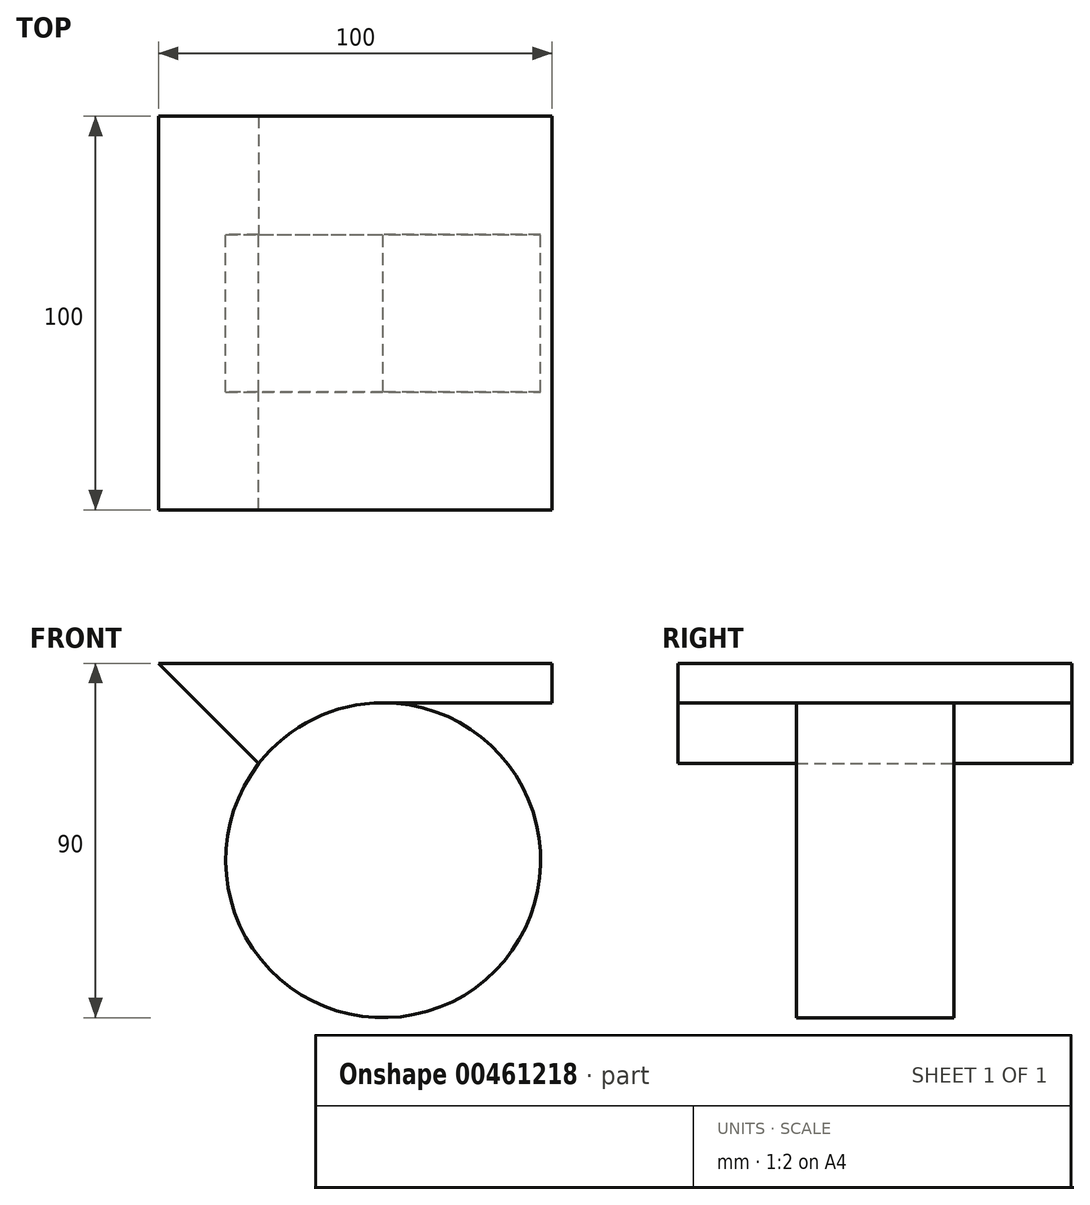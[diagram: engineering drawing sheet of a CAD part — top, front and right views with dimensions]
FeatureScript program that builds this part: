
annotation { "Feature Type Name" : "Feature", "Feature Type Description" : "" }
export const myFeature = defineFeature(function(context is Context, id is Id, definition is map)
    precondition{}
    {
        {
            var Q0;
            Q0=qCreatedBy(makeId("Front.planeOp"),FACE);
            var sketch = newSketch(context, id + "F0", { "sketchPlane" : qUnion([Q0])});
            skArc(sketch, "E0", {"start": v(-31.58, 24.54) * mm, "mid": v(17.58, -35.93) * mm, "end": v(0, 40) * mm});
            skLineSegment(sketch, "E1", {"start": v(0, 40) * mm, "end": v(42.96, 40) * mm});
            skLineSegment(sketch, "E2", {"start": v(42.96, 40) * mm, "end": v(42.96, 50) * mm});
            skLineSegment(sketch, "E3", {"start": v(42.96, 50) * mm, "end": v(-57.04, 50) * mm});
            skLineSegment(sketch, "E4", {"start": v(-57.04, 50) * mm, "end": v(-31.58, 24.54) * mm});
            skSolve(sketch);
        }
        {
            var Q0;
            Q0=makeQuery(id+"F0.imprint","IMPRINT",FACE,{"disambiguationData":[TD([[makeQuery(id+"F0.imprint","IMPRINT",EDGE,{"derivedFrom":sQuery(id+"F0.wireOp",EDGE,"E0")}),1.0]])]});
            extrude(context, id + "F1", {"entities" : qUnion([Q0]), "depth" : 40 * mm});
        }
        {
            var Q0;
            Q0=makeQuery(id+"F1.opExtrude","CAP_FACE",FACE,{"disambiguationData":[OSD([sQuery(id+"F0.wireOp",EDGE,"E0"),sQuery(id+"F0.wireOp",EDGE,"E1"),sQuery(id+"F0.wireOp",EDGE,"E2"),sQuery(id+"F0.wireOp",EDGE,"E3"),sQuery(id+"F0.wireOp",EDGE,"E4")])],"isStart":false});
            var sketch = newSketch(context, id + "F2", { "sketchPlane" : qUnion([Q0])});
            skCircle(sketch, "E5", {"center": v(0, 0) * mm, "radius": 40 * mm});
            skLineSegment(sketch, "E6", {"start": v(0, 40) * mm, "end": v(42.96, 40) * mm});
            skLineSegment(sketch, "E7", {"start": v(42.96, 40) * mm, "end": v(42.96, 50) * mm});
            skLineSegment(sketch, "E8", {"start": v(42.96, 50) * mm, "end": v(-57.04, 50) * mm});
            skLineSegment(sketch, "E9", {"start": v(-57.04, 50) * mm, "end": v(-31.58, 24.54) * mm});
            skSolve(sketch);
        }
        {
            var Q0;
            {var subQ0=sQuery(id+"F2.wireOp",EDGE,"E6");Q0=makeQuery(id+"F2.imprint","IMPRINT",FACE,{"disambiguationData":[TD([[makeQuery(id+"F2.imprint","IMPRINT",EDGE,{"derivedFrom":subQ0}),1.0]])]});}
            extrude(context, id + "F3", {"entities" : qUnion([Q0]), "operationType" : NewBodyOperationType.ADD, "depth" : 30 * mm});
        }
        {
            var Q0;
            Q0=makeQuery(id+"F1.opExtrude","CAP_FACE",FACE,{"disambiguationData":[OSD([sQuery(id+"F0.wireOp",EDGE,"E0"),sQuery(id+"F0.wireOp",EDGE,"E1"),sQuery(id+"F0.wireOp",EDGE,"E2"),sQuery(id+"F0.wireOp",EDGE,"E3"),sQuery(id+"F0.wireOp",EDGE,"E4")])],"isStart":true});
            var sketch = newSketch(context, id + "F4", { "sketchPlane" : qUnion([Q0])});
            skCircle(sketch, "E10", {"center": v(0, 0) * mm, "radius": 40 * mm});
            skSolve(sketch);
        }
        {
            var Q0;
            Q0=makeQuery(id+"F4.imprint","IMPRINT",FACE,{"disambiguationData":[TD([[makeQuery(id+"F4.imprint","IMPRINT",EDGE,{"disambiguationData":[OD(1.0)],"derivedFrom":sQuery(id+"F4.wireOp",EDGE,"E10")}),-1.0]])]});
            extrude(context, id + "F5", {"entities" : qUnion([Q0]), "operationType" : NewBodyOperationType.ADD, "depth" : 30 * mm});
        }
    });
